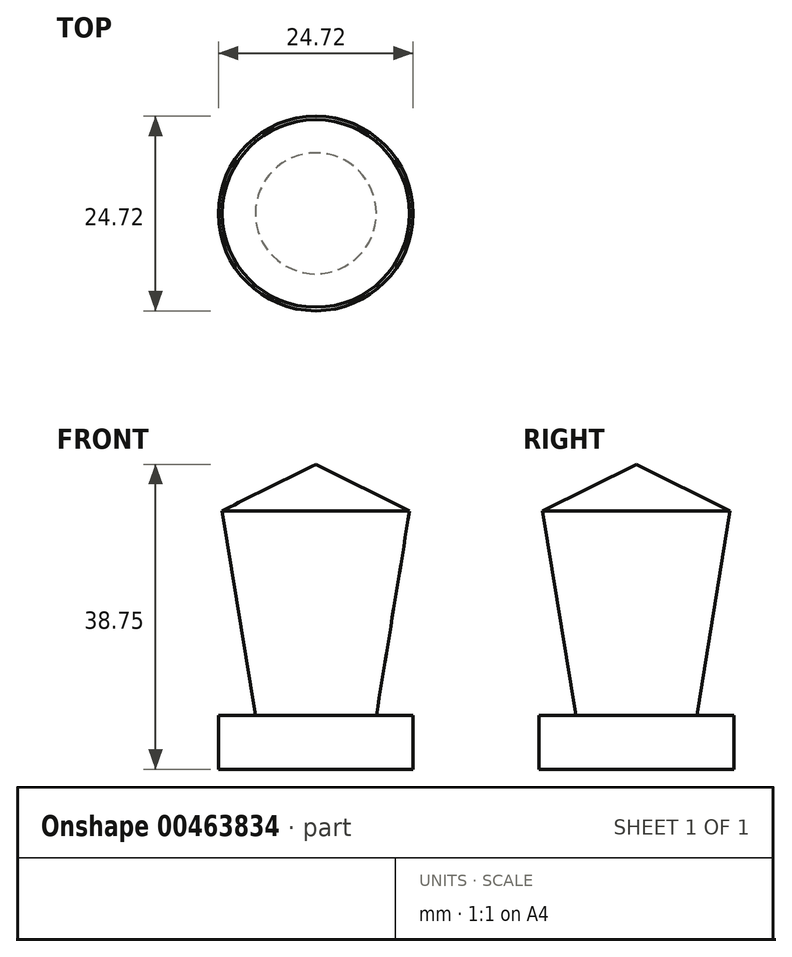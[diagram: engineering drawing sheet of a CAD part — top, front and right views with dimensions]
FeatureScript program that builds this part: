
annotation { "Feature Type Name" : "Feature", "Feature Type Description" : "" }
export const myFeature = defineFeature(function(context is Context, id is Id, definition is map)
    precondition{}
    {
        {
            var Q0;
            Q0=qCreatedBy(makeId("Front.planeOp"),FACE);
            var sketch = newSketch(context, id + "F0", { "sketchPlane" : qUnion([Q0])});
            skLineSegment(sketch, "E0", {"start": v(0, 17.87) * mm, "end": v(0, -20.88) * mm});
            skLineSegment(sketch, "E1", {"start": v(0, -20.88) * mm, "end": v(12.36, -20.88) * mm});
            skLineSegment(sketch, "E2", {"start": v(12.36, -20.88) * mm, "end": v(12.36, -14.04) * mm});
            skLineSegment(sketch, "E3", {"start": v(12.36, -14.04) * mm, "end": v(7.68, -14.04) * mm});
            skLineSegment(sketch, "E4", {"start": v(7.68, -14.04) * mm, "end": v(11.9, 11.96) * mm});
            skLineSegment(sketch, "E5", {"start": v(0, 17.87) * mm, "end": v(11.9, 11.96) * mm});
            skSolve(sketch);
        }
        {
            var Q0;
            Q0 = qSketchRegion(id + "F0", true);
            var Q1;
            Q1=sQuery(id+"F0.wireOp",EDGE,"E0");
            revolve(context, id + "F1", {"entities" : qUnion([Q0]), "axis" : qUnion([Q1]), "revolveType" : RevolveType.FULL});
        }
    });
